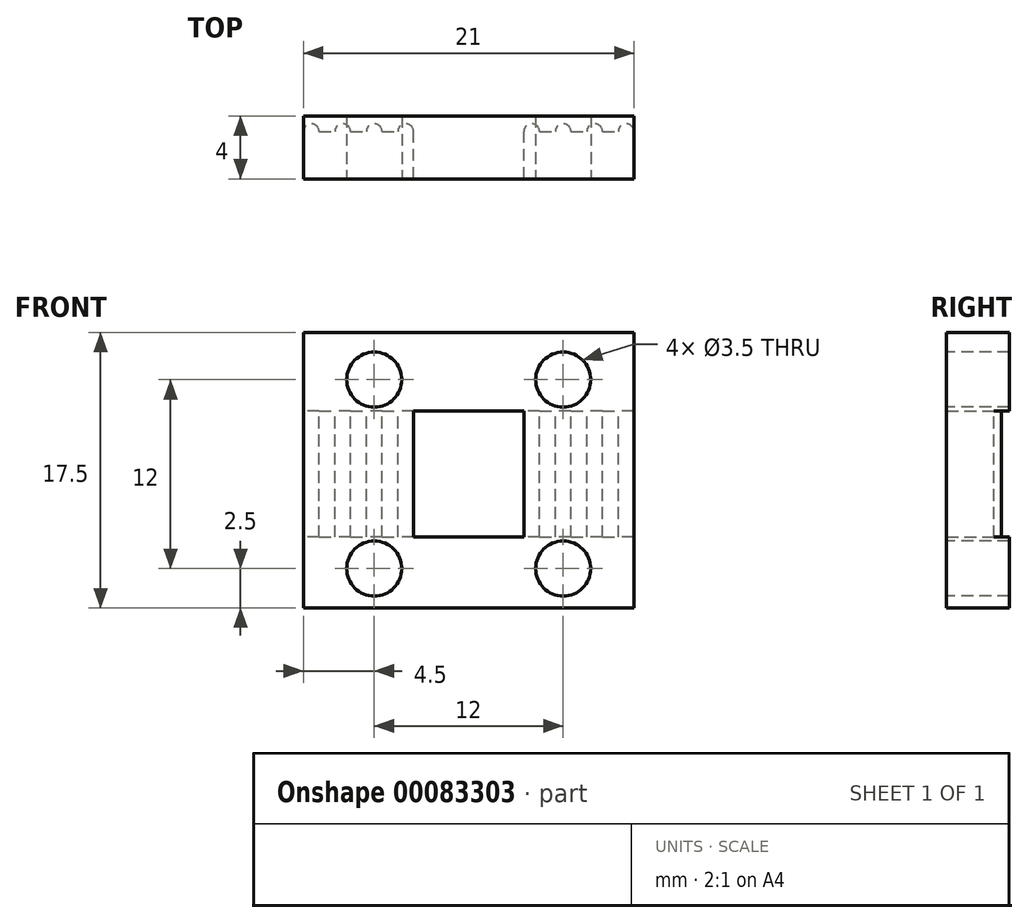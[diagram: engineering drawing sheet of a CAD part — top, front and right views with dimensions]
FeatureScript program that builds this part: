
annotation { "Feature Type Name" : "Feature", "Feature Type Description" : "" }
export const myFeature = defineFeature(function(context is Context, id is Id, definition is map)
    precondition{}
    {
        {
            var Q0;
            Q0=qCreatedBy(makeId("Top.planeOp"),FACE);
            cPlane(context, id + "F0", {"entities" : qUnion([Q0]), "cplaneType" : CPlaneType.OFFSET, "offset" : 8.5 * mm, "width" : 150 * mm, "height" : 150 * mm});
        }
        {
            var Q0;
            Q0=qCreatedBy(makeId("Top.planeOp"),FACE);
            var sketch = newSketch(context, id + "F1", { "sketchPlane" : qUnion([Q0])});
            skLineSegment(sketch, "E0.bottom", {"start": v(10.5, 2) * mm, "end": v(-10.5, 2) * mm});
            skLineSegment(sketch, "E0.top", {"start": v(10.5, -2) * mm, "end": v(-10.5, -2) * mm});
            skLineSegment(sketch, "E0.left", {"start": v(10.5, 2) * mm, "end": v(10.5, -2) * mm});
            skLineSegment(sketch, "E0.right", {"start": v(-10.5, 2) * mm, "end": v(-10.5, -2) * mm});
            skPoint(sketch, "E0.middle", {"position": v(0, 0) * mm});
            skSolve(sketch);
        }
        {
            var Q0;
            Q0=qSketchRegion(id+"F1",true);
            extrude(context, id + "F2", {"entities" : qUnion([Q0]), "depth" : 17.5 * mm});
        }
        {
            var Q0;
            Q0=makeQuery(id+"F2.opExtrude","SWEPT_FACE",FACE,{"disambiguationData":[OSD([sQuery(id+"F1.wireOp",EDGE,"E0.top")])]});
            var sketch = newSketch(context, id + "F3", { "sketchPlane" : qUnion([Q0])});
            skCircle(sketch, "E1", {"center": v(-6, 14.5) * mm, "radius": 1.75 * mm});
            skCircle(sketch, "E2", {"center": v(6, 14.5) * mm, "radius": 1.75 * mm});
            skLineSegment(sketch, "E3.bottom", {"start": v(6, 14.5) * mm, "end": v(-6, 14.5) * mm, "construction": true});
            skLineSegment(sketch, "E3.top", {"start": v(6, 2.5) * mm, "end": v(-6, 2.5) * mm, "construction": true});
            skLineSegment(sketch, "E3.left", {"start": v(6, 14.5) * mm, "end": v(6, 2.5) * mm, "construction": true});
            skLineSegment(sketch, "E3.right", {"start": v(-6, 14.5) * mm, "end": v(-6, 2.5) * mm, "construction": true});
            skCircle(sketch, "E4", {"center": v(6, 2.5) * mm, "radius": 1.75 * mm});
            skCircle(sketch, "E5", {"center": v(-6, 2.5) * mm, "radius": 1.75 * mm});
            skSolve(sketch);
        }
        {
            var Q0;
            Q0=qSketchRegion(id+"F3",true);
            extrude(context, id + "F4", {"entities" : qUnion([Q0]), "operationType" : NewBodyOperationType.REMOVE, "endBound" : BoundingType.THROUGH_ALL, "oppositeDirection" : true, "depth" : 25 * mm});
        }
        {
            var Q0;
            Q0=qCreatedBy(id+"F0.planeOp",FACE);
            var sketch = newSketch(context, id + "F5", { "sketchPlane" : qUnion([Q0])});
            skLineSegment(sketch, "E6.bottom", {"start": v(-10.5, 2) * mm, "end": v(10.5, 2) * mm});
            skLineSegment(sketch, "E6.top", {"start": v(-10.5, 1) * mm, "end": v(10.5, 1) * mm});
            skLineSegment(sketch, "E6.left", {"start": v(-10.5, 1) * mm, "end": v(-10.5, 2) * mm});
            skLineSegment(sketch, "E6.right", {"start": v(10.5, 1) * mm, "end": v(10.5, 2) * mm});
            skSolve(sketch);
        }
        {
            var Q0;
            Q0=qSketchRegion(id+"F5",true);
            extrude(context, id + "F6", {"entities" : qUnion([Q0]), "operationType" : NewBodyOperationType.REMOVE, "endBound" : BoundingType.SYMMETRIC, "oppositeDirection" : true, "depth" : 8 * mm});
        }
        {
            var Q0;
            Q0=qCreatedBy(id+"F0.planeOp",FACE);
            var sketch = newSketch(context, id + "F7", { "sketchPlane" : qUnion([Q0])});
            skCircle(sketch, "E7", {"center": v(10, 1) * mm, "radius": 0.5 * mm});
            skCircle(sketch, "E8.1.0.0", {"center": v(8, 1) * mm, "radius": 0.5 * mm});
            skCircle(sketch, "E8.2.0.0", {"center": v(6, 1) * mm, "radius": 0.5 * mm});
            skCircle(sketch, "E8.3.0.0", {"center": v(4, 1) * mm, "radius": 0.5 * mm});
            skCircle(sketch, "E8.4.0.0", {"center": v(2, 1) * mm, "radius": 0.5 * mm});
            skCircle(sketch, "E8.5.0.0", {"center": v(0, 1) * mm, "radius": 0.5 * mm});
            skCircle(sketch, "E8.6.0.0", {"center": v(-2, 1) * mm, "radius": 0.5 * mm});
            skCircle(sketch, "E8.7.0.0", {"center": v(-4, 1) * mm, "radius": 0.5 * mm});
            skCircle(sketch, "E8.8.0.0", {"center": v(-6, 1) * mm, "radius": 0.5 * mm});
            skCircle(sketch, "E8.9.0.0", {"center": v(-8, 1) * mm, "radius": 0.5 * mm});
            skCircle(sketch, "E8.10.0.0", {"center": v(-10, 1) * mm, "radius": 0.5 * mm});
            skLineSegment(sketch, "E8.direction1", {"start": v(10, 1) * mm, "end": v(8, 1) * mm, "construction": true});
            skSolve(sketch);
        }
        {
            var Q0;
            Q0=qSketchRegion(id+"F7",true);
            extrude(context, id + "F8", {"entities" : qUnion([Q0]), "operationType" : NewBodyOperationType.ADD, "endBound" : BoundingType.SYMMETRIC, "oppositeDirection" : true, "depth" : 8 * mm});
        }
        {
            var Q0;
            Q0=qCreatedBy(id+"F0.planeOp",FACE);
            var sketch = newSketch(context, id + "F9", { "sketchPlane" : qUnion([Q0])});
            skLineSegment(sketch, "E9.bottom", {"start": v(3.5, -3.41) * mm, "end": v(-3.5, -3.41) * mm});
            skLineSegment(sketch, "E9.top", {"start": v(3.5, 3.41) * mm, "end": v(-3.5, 3.41) * mm});
            skLineSegment(sketch, "E9.left", {"start": v(3.5, -3.41) * mm, "end": v(3.5, 3.41) * mm});
            skLineSegment(sketch, "E9.right", {"start": v(-3.5, -3.41) * mm, "end": v(-3.5, 3.41) * mm});
            skPoint(sketch, "E9.middle", {"position": v(0, 0) * mm});
            skSolve(sketch);
        }
        {
            var Q0;
            Q0=qSketchRegion(id+"F9",true);
            extrude(context, id + "F10", {"entities" : qUnion([Q0]), "operationType" : NewBodyOperationType.REMOVE, "endBound" : BoundingType.SYMMETRIC, "oppositeDirection" : true, "depth" : 8 * mm});
        }
    });
